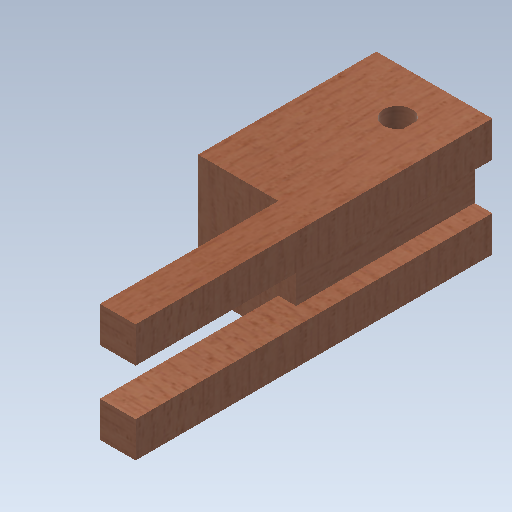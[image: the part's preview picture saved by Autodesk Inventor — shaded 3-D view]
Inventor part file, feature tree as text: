
AUTODESK INVENTOR PART (.ipt)
format: ipt  version: 2021.3 (Build 253353000, 353)  size: 241,152 bytes
history: native  units: mm
features: extrude x3, sketch x3, reference x1
ambient origin geometry x8: Origin, YZ Plane, XZ Plane, XY Plane, X Axis, Y Axis, Z Axis, Center Point
bodies: Solid1 (feature_tree)
feature tree (7):
  extrude  "Extrusion1"  Depth=66.0mm
  extrude  "Extrusion2"  Depth=100.0mm TaperAngle=0.0deg
  extrude  "Extrusion3"  Depth=20.0mm
  sketch  "Sketch1"  dims[d0=55.0mm d1=66.0mm]
  sketch  "Sketch2"  dims[d2=100.0mm d3=0.0mm d4=70.0mm d5=0.0mm]
  reference  "Reference1"
  sketch  "Sketch3"  dims[d6=200.0mm d7=20.0mm d8=200.0mm d9=20.0mm d10=20.0mm d11=0.0mm]
